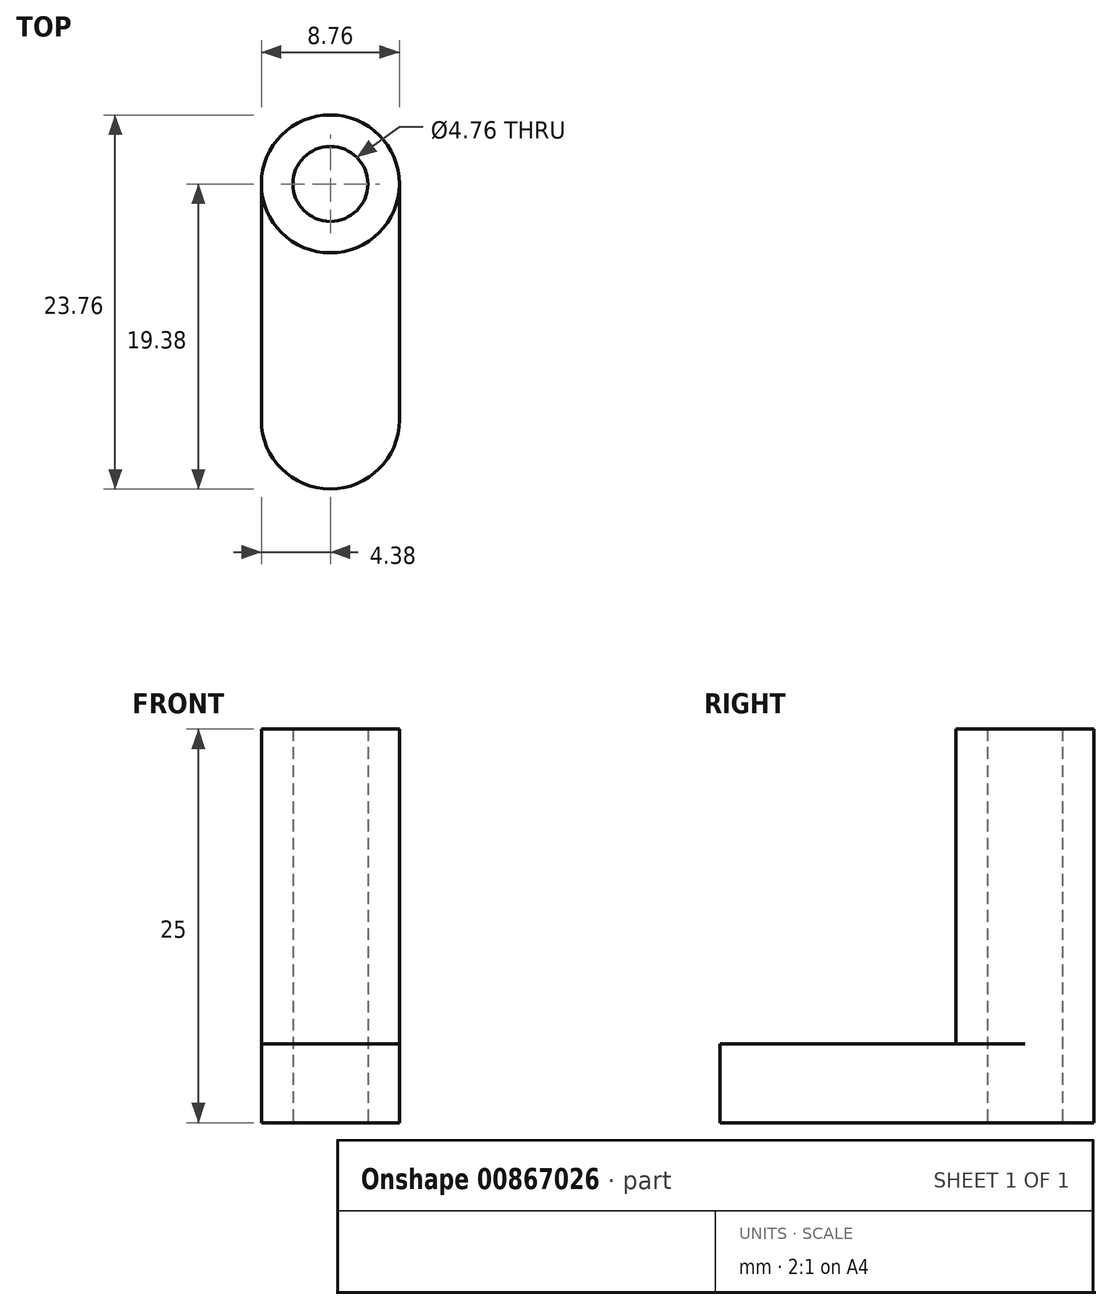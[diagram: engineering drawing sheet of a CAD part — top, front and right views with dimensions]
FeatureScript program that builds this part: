
annotation { "Feature Type Name" : "Feature", "Feature Type Description" : "" }
export const myFeature = defineFeature(function(context is Context, id is Id, definition is map)
    precondition{}
    {
        {
            var Q0;
            Q0=qCreatedBy(makeId("Top.planeOp"),FACE);
            var sketch = newSketch(context, id + "F0", { "sketchPlane" : qUnion([Q0])});
            skCircle(sketch, "E0", {"center": v(0, 0) * mm, "radius": 2.38 * mm});
            skCircle(sketch, "E1", {"center": v(0, 0) * mm, "radius": 4.38 * mm});
            skSolve(sketch);
        }
        {
            var Q0;
            Q0 = qSketchRegion(id + "F0", true);
            extrude(context, id + "F1", {"entities" : qUnion([Q0]), "depth" : 20 * mm, "offsetDistance" : 25 * mm});
        }
        {
            var Q0;
            Q0=makeQuery(id+"F1.opExtrude","CAP_FACE",FACE,{"disambiguationData":[OSD([sQuery(id+"F0.wireOp",EDGE,"E0"),sQuery(id+"F0.wireOp",EDGE,"E1")])],"isStart":true});
            var sketch = newSketch(context, id + "F2", { "sketchPlane" : qUnion([Q0])});
            skArc(sketch, "E2", {"start": v(-4.38, 0) * mm, "mid": v(0, -4.38) * mm, "end": v(4.38, 0) * mm});
            skLineSegment(sketch, "E3", {"start": v(4.38, 0) * mm, "end": v(4.38, 15) * mm});
            skLineSegment(sketch, "E4.MirrorCS", {"start": v(-4.38, 0) * mm, "end": v(-4.38, 15) * mm});
            skArc(sketch, "E5", {"start": v(4.38, 15) * mm, "mid": v(0, 19.38) * mm, "end": v(-4.38, 15) * mm});
            skCircle(sketch, "E6", {"center": v(0, 0) * mm, "radius": 2.38 * mm});
            skSolve(sketch);
        }
        {
            var Q0;
            Q0 = qSketchRegion(id + "F2", true);
            extrude(context, id + "F3", {"entities" : qUnion([Q0]), "operationType" : NewBodyOperationType.ADD, "depth" : 5 * mm, "offsetDistance" : 25 * mm});
        }
    });
